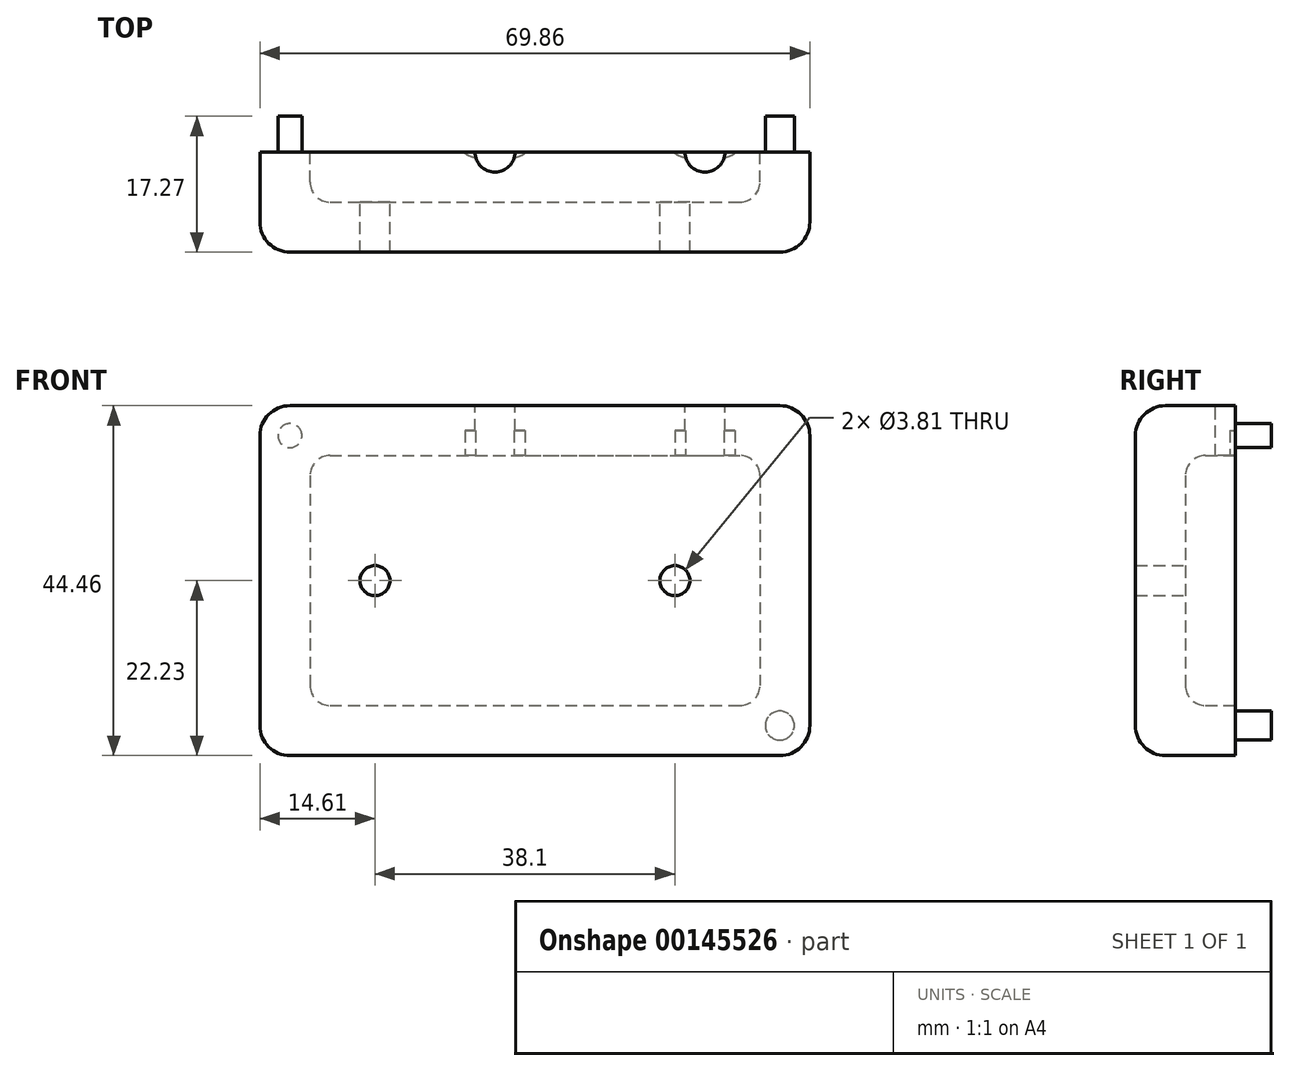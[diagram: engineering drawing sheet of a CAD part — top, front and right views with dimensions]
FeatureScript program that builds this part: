
annotation { "Feature Type Name" : "Feature", "Feature Type Description" : "" }
export const myFeature = defineFeature(function(context is Context, id is Id, definition is map)
    precondition{}
    {
        {
            var Q0;
            Q0=qCreatedBy(makeId("Front.planeOp"),FACE);
            var sketch = newSketch(context, id + "F0", { "sketchPlane" : qUnion([Q0])});
            skLineSegment(sketch, "E0.bottom", {"start": v(-34.92, 22.23) * mm, "end": v(34.93, 22.23) * mm});
            skLineSegment(sketch, "E0.top", {"start": v(-34.93, -22.22) * mm, "end": v(34.92, -22.22) * mm});
            skLineSegment(sketch, "E0.left", {"start": v(-34.93, 22.23) * mm, "end": v(-34.93, -22.22) * mm});
            skLineSegment(sketch, "E0.right", {"start": v(34.93, 22.23) * mm, "end": v(34.92, -22.22) * mm});
            skPoint(sketch, "E0.middle", {"position": v(0, 0) * mm});
            skSolve(sketch);
        }
        {
            var Q0;
            Q0=qSketchRegion(id+"F0",true);
            extrude(context, id + "F1", {"entities" : qUnion([Q0]), "depth" : 12.7 * mm});
        }
        {
            var Q0;
            Q0=makeQuery(id+"F1.opExtrude","CAP_FACE",FACE,{"disambiguationData":[OSD([sQuery(id+"F0.wireOp",EDGE,"LqZrlxkr-7yzX-vFk0-uJjs-JSWsayYtNQzV"),sQuery(id+"F0.wireOp",EDGE,"5r0xhfTH-CSDF-mAA5-pvvG-RkQlhuwyMzcQ"),sQuery(id+"F0.wireOp",EDGE,"ef0f229b-e142-484f-bc61-ead6fe579b0b"),sQuery(id+"F0.wireOp",EDGE,"6fDFFfjc-EMaK-PeL7-7E0k-bSpFbJlcJFc0"),sQuery(id+"F0.wireOp",EDGE,"250b579a-bc1c-4dc2-aff8-3702901d077b0.MirrorCS"),sQuery(id+"F0.wireOp",EDGE,"42722c59-2561-4240-b2ed-f956cca0e4cb0.MirrorCS"),sQuery(id+"F0.wireOp",EDGE,"67368090-a0b9-42d5-ac4e-b1d2cad05f430.MirrorCS"),sQuery(id+"F0.wireOp",EDGE,"083a49a4-ea0b-41bf-8828-168f702bc1710.MirrorCS")])],"isStart":true});
            var Q1;
            Q1=makeQuery(id+"F1.opExtrude","CAP_FACE",FACE,{"disambiguationData":[OSD([sQuery(id+"F0.wireOp",EDGE,"E0.bottom"),sQuery(id+"F0.wireOp",EDGE,"E0.top"),sQuery(id+"F0.wireOp",EDGE,"E0.left"),sQuery(id+"F0.wireOp",EDGE,"E0.right")])],"isStart":true});
            shell(context, id + "F2", {"entities" : qUnion([Q0, Q1]), "thickness" : 6.35 * mm});
        }
        {
            var Q0;
            Q0=makeQuery(id+"F1.opExtrude","CAP_FACE",FACE,{"disambiguationData":[OSD([sQuery(id+"F0.wireOp",EDGE,"LqZrlxkr-7yzX-vFk0-uJjs-JSWsayYtNQzV"),sQuery(id+"F0.wireOp",EDGE,"5r0xhfTH-CSDF-mAA5-pvvG-RkQlhuwyMzcQ"),sQuery(id+"F0.wireOp",EDGE,"ef0f229b-e142-484f-bc61-ead6fe579b0b"),sQuery(id+"F0.wireOp",EDGE,"6fDFFfjc-EMaK-PeL7-7E0k-bSpFbJlcJFc0"),sQuery(id+"F0.wireOp",EDGE,"250b579a-bc1c-4dc2-aff8-3702901d077b0.MirrorCS"),sQuery(id+"F0.wireOp",EDGE,"42722c59-2561-4240-b2ed-f956cca0e4cb0.MirrorCS"),sQuery(id+"F0.wireOp",EDGE,"67368090-a0b9-42d5-ac4e-b1d2cad05f430.MirrorCS"),sQuery(id+"F0.wireOp",EDGE,"083a49a4-ea0b-41bf-8828-168f702bc1710.MirrorCS")])],"isStart":false});
            var Q1;
            Q1=makeQuery(id+"F1.opExtrude","SWEPT_EDGE",EDGE,{"disambiguationData":[OSD([sQuery(id+"F0.wireOp",EDGE,"LqZrlxkr-7yzX-vFk0-uJjs-JSWsayYtNQzV"),sQuery(id+"F0.wireOp",EDGE,"5r0xhfTH-CSDF-mAA5-pvvG-RkQlhuwyMzcQ")])]});
            var Q2;
            Q2=makeQuery(id+"F1.opExtrude","SWEPT_EDGE",EDGE,{"disambiguationData":[OSD([sQuery(id+"F0.wireOp",EDGE,"5r0xhfTH-CSDF-mAA5-pvvG-RkQlhuwyMzcQ"),sQuery(id+"F0.wireOp",EDGE,"ef0f229b-e142-484f-bc61-ead6fe579b0b")])]});
            var Q3;
            Q3=makeQuery(id+"F1.opExtrude","SWEPT_EDGE",EDGE,{"disambiguationData":[OSD([sQuery(id+"F0.wireOp",EDGE,"ef0f229b-e142-484f-bc61-ead6fe579b0b"),sQuery(id+"F0.wireOp",EDGE,"6fDFFfjc-EMaK-PeL7-7E0k-bSpFbJlcJFc0")])]});
            var Q4;
            Q4=makeQuery(id+"F1.opExtrude","SWEPT_EDGE",EDGE,{"disambiguationData":[OSD([sQuery(id+"F0.wireOp",EDGE,"250b579a-bc1c-4dc2-aff8-3702901d077b0.MirrorCS"),sQuery(id+"F0.wireOp",EDGE,"42722c59-2561-4240-b2ed-f956cca0e4cb0.MirrorCS")])]});
            var Q5;
            Q5=makeQuery(id+"F1.opExtrude","SWEPT_EDGE",EDGE,{"disambiguationData":[OSD([sQuery(id+"F0.wireOp",EDGE,"250b579a-bc1c-4dc2-aff8-3702901d077b0.MirrorCS"),sQuery(id+"F0.wireOp",EDGE,"083a49a4-ea0b-41bf-8828-168f702bc1710.MirrorCS")])]});
            var Q6;
            Q6=makeQuery(id+"F1.opExtrude","SWEPT_EDGE",EDGE,{"disambiguationData":[OSD([sQuery(id+"F0.wireOp",EDGE,"67368090-a0b9-42d5-ac4e-b1d2cad05f430.MirrorCS"),sQuery(id+"F0.wireOp",EDGE,"083a49a4-ea0b-41bf-8828-168f702bc1710.MirrorCS")])]});
            var Q7;
            Q7=makeQuery(id+"F1.opExtrude","SWEPT_EDGE",EDGE,{"disambiguationData":[OSD([sQuery(id+"F0.wireOp",EDGE,"E0.top"),sQuery(id+"F0.wireOp",EDGE,"E0.right")])]});
            var Q8;
            Q8=makeQuery(id+"F1.opExtrude","CAP_EDGE",EDGE,{"disambiguationData":[OSD([sQuery(id+"F0.wireOp",EDGE,"E0.right")])],"isStart":false});
            var Q9;
            Q9=makeQuery(id+"F1.opExtrude","CAP_EDGE",EDGE,{"disambiguationData":[OSD([sQuery(id+"F0.wireOp",EDGE,"E0.top")])],"isStart":false});
            var Q10;
            Q10=makeQuery(id+"F1.opExtrude","CAP_EDGE",EDGE,{"disambiguationData":[OSD([sQuery(id+"F0.wireOp",EDGE,"E0.left")])],"isStart":false});
            var Q11;
            Q11=makeQuery(id+"F1.opExtrude","CAP_EDGE",EDGE,{"disambiguationData":[OSD([sQuery(id+"F0.wireOp",EDGE,"E0.bottom")])],"isStart":false});
            var Q12;
            Q12=makeQuery(id+"F1.opExtrude","SWEPT_EDGE",EDGE,{"disambiguationData":[OSD([sQuery(id+"F0.wireOp",EDGE,"E0.bottom"),sQuery(id+"F0.wireOp",EDGE,"E0.left")])]});
            var Q13;
            Q13=makeQuery(id+"F1.opExtrude","SWEPT_EDGE",EDGE,{"disambiguationData":[OSD([sQuery(id+"F0.wireOp",EDGE,"E0.bottom"),sQuery(id+"F0.wireOp",EDGE,"E0.right")])]});
            var Q14;
            Q14=makeQuery(id+"F1.opExtrude","SWEPT_EDGE",EDGE,{"disambiguationData":[OSD([sQuery(id+"F0.wireOp",EDGE,"E0.top"),sQuery(id+"F0.wireOp",EDGE,"E0.left")])]});
            fillet(context, id + "F3", {"entities" : qUnion([Q0, Q1, Q2, Q3, Q4, Q5, Q6, Q7, Q8, Q9, Q10, Q11, Q12, Q13, Q14]), "radius" : 3.8 * mm, "tangentPropagation" : true, "allowEdgeOverflow" : false});
        }
        {
            var Q0;
            Q0=makeQuery(id+"F2.opShell","OFFSET_FACE",FACE,{"disambiguationData":[OSD([sQuery(id+"F0.wireOp",EDGE,"E0.bottom"),sQuery(id+"F0.wireOp",EDGE,"E0.top"),sQuery(id+"F0.wireOp",EDGE,"E0.left"),sQuery(id+"F0.wireOp",EDGE,"E0.right")])]});
            var Q1;
            Q1=makeQuery(id+"F2.opShell","OFFSET_EDGE",EDGE,{"disambiguationData":[OSD([sQuery(id+"F0.wireOp",EDGE,"E0.top"),sQuery(id+"F0.wireOp",EDGE,"E0.left")])]});
            var Q2;
            Q2=makeQuery(id+"F2.opShell","OFFSET_EDGE",EDGE,{"disambiguationData":[OSD([sQuery(id+"F0.wireOp",EDGE,"E0.top"),sQuery(id+"F0.wireOp",EDGE,"E0.right")])]});
            var Q3;
            Q3=makeQuery(id+"F2.opShell","OFFSET_EDGE",EDGE,{"disambiguationData":[OSD([sQuery(id+"F0.wireOp",EDGE,"E0.bottom"),sQuery(id+"F0.wireOp",EDGE,"E0.right")])]});
            var Q4;
            Q4=makeQuery(id+"F2.opShell","OFFSET_EDGE",EDGE,{"disambiguationData":[OSD([sQuery(id+"F0.wireOp",EDGE,"E0.bottom"),sQuery(id+"F0.wireOp",EDGE,"E0.left")])]});
            fillet(context, id + "F4", {"entities" : qUnion([Q0, Q1, Q2, Q3, Q4]), "radius" : 2.54 * mm, "tangentPropagation" : true, "allowEdgeOverflow" : false});
        }
        {
            var Q0;
            Q0=makeQuery(id+"F1.opExtrude","CAP_FACE",FACE,{"disambiguationData":[OSD([sQuery(id+"F0.wireOp",EDGE,"E0.bottom"),sQuery(id+"F0.wireOp",EDGE,"E0.top"),sQuery(id+"F0.wireOp",EDGE,"E0.left"),sQuery(id+"F0.wireOp",EDGE,"E0.right")])],"isStart":true});
            var sketch = newSketch(context, id + "F5", { "sketchPlane" : qUnion([Q0])});
            skCircle(sketch, "E1", {"center": v(31.12, 18.42) * mm, "radius": 1.52 * mm});
            skCircle(sketch, "E2", {"center": v(-31.12, -18.41) * mm, "radius": 1.84 * mm});
            skSolve(sketch);
        }
        {
            var Q0;
            Q0 = qSketchRegion(id + "F5", true);
            extrude(context, id + "F6", {"entities" : qUnion([Q0]), "operationType" : NewBodyOperationType.ADD, "depth" : 4.57 * mm});
        }
        {
            var Q0;
            Q0=makeQuery(id+"F2.opShell","OFFSET_FACE",FACE,{"disambiguationData":[OSD([sQuery(id+"F0.wireOp",EDGE,"E0.bottom"),sQuery(id+"F0.wireOp",EDGE,"E0.top"),sQuery(id+"F0.wireOp",EDGE,"E0.left"),sQuery(id+"F0.wireOp",EDGE,"E0.right")])]});
            var sketch = newSketch(context, id + "F7", { "sketchPlane" : qUnion([Q0])});
            skCircle(sketch, "E3", {"center": v(20.32, 0) * mm, "radius": 1.9 * mm});
            skCircle(sketch, "E4", {"center": v(-17.78, 0) * mm, "radius": 1.9 * mm});
            skSolve(sketch);
        }
        {
            var Q0;
            Q0=qSketchRegion(id+"F7",true);
            extrude(context, id + "F8", {"entities" : qUnion([Q0]), "operationType" : NewBodyOperationType.REMOVE, "endBound" : BoundingType.UP_TO_NEXT, "oppositeDirection" : true, "depth" : 25.4 * mm});
        }
        {
            var Q0;
            Q0=makeQuery(id+"F1.opExtrude","SWEPT_FACE",FACE,{"disambiguationData":[OSD([sQuery(id+"F0.wireOp",EDGE,"E0.bottom")])]});
            var sketch = newSketch(context, id + "F9", { "sketchPlane" : qUnion([Q0])});
            skLineSegment(sketch, "E5", {"start": v(-5.08, 15.95) * mm, "end": v(-5.08, -26.98) * mm, "construction": true});
            skLineSegment(sketch, "E6", {"start": v(21.6, 16.87) * mm, "end": v(21.6, -27.9) * mm, "construction": true});
            skLineSegment(sketch, "E7", {"start": v(-42.21, 0) * mm, "end": v(51.68, 0) * mm, "construction": true});
            skCircle(sketch, "E8", {"center": v(-5.08, 0) * mm, "radius": 2.54 * mm});
            skCircle(sketch, "E9", {"center": v(21.6, 0) * mm, "radius": 2.54 * mm});
            skSolve(sketch);
        }
        {
            var Q0;
            Q0 = qSketchRegion(id + "F9", true);
            var Q1;
            Q1=makeQuery(id+"F2.opShell","OFFSET_FACE",FACE,{"disambiguationData":[OSD([sQuery(id+"F0.wireOp",EDGE,"E0.bottom")])]});
            extrude(context, id + "F10", {"entities" : qUnion([Q0]), "operationType" : NewBodyOperationType.REMOVE, "endBound" : BoundingType.UP_TO_SURFACE, "oppositeDirection" : true, "endBoundEntityFace" : qUnion([Q1]), "depth" : 25.4 * mm});
        }
        {
            var Q0;
            Q0=makeQuery(id+"F2.opShell","OFFSET_FACE",FACE,{"disambiguationData":[OSD([sQuery(id+"F0.wireOp",EDGE,"E0.bottom")])]});
            var sketch = newSketch(context, id + "F11", { "sketchPlane" : qUnion([Q0])});
            skEllipse(sketch, "E10", {"center": v(-5.08, 0) * mm, "majorRadius": 3.81 * mm, "minorRadius": 0.95 * mm, "majorAxis": v(-1, 0)});
            skEllipse(sketch, "E11", {"center": v(21.6, 0) * mm, "majorRadius": 3.81 * mm, "minorRadius": 0.95 * mm, "majorAxis": v(-1, 0)});
            skSolve(sketch);
        }
        {
            var Q0;
            Q0 = qSketchRegion(id + "F11", true);
            extrude(context, id + "F12", {"entities" : qUnion([Q0]), "operationType" : NewBodyOperationType.REMOVE, "oppositeDirection" : true, "depth" : 3.17 * mm});
        }
    });
